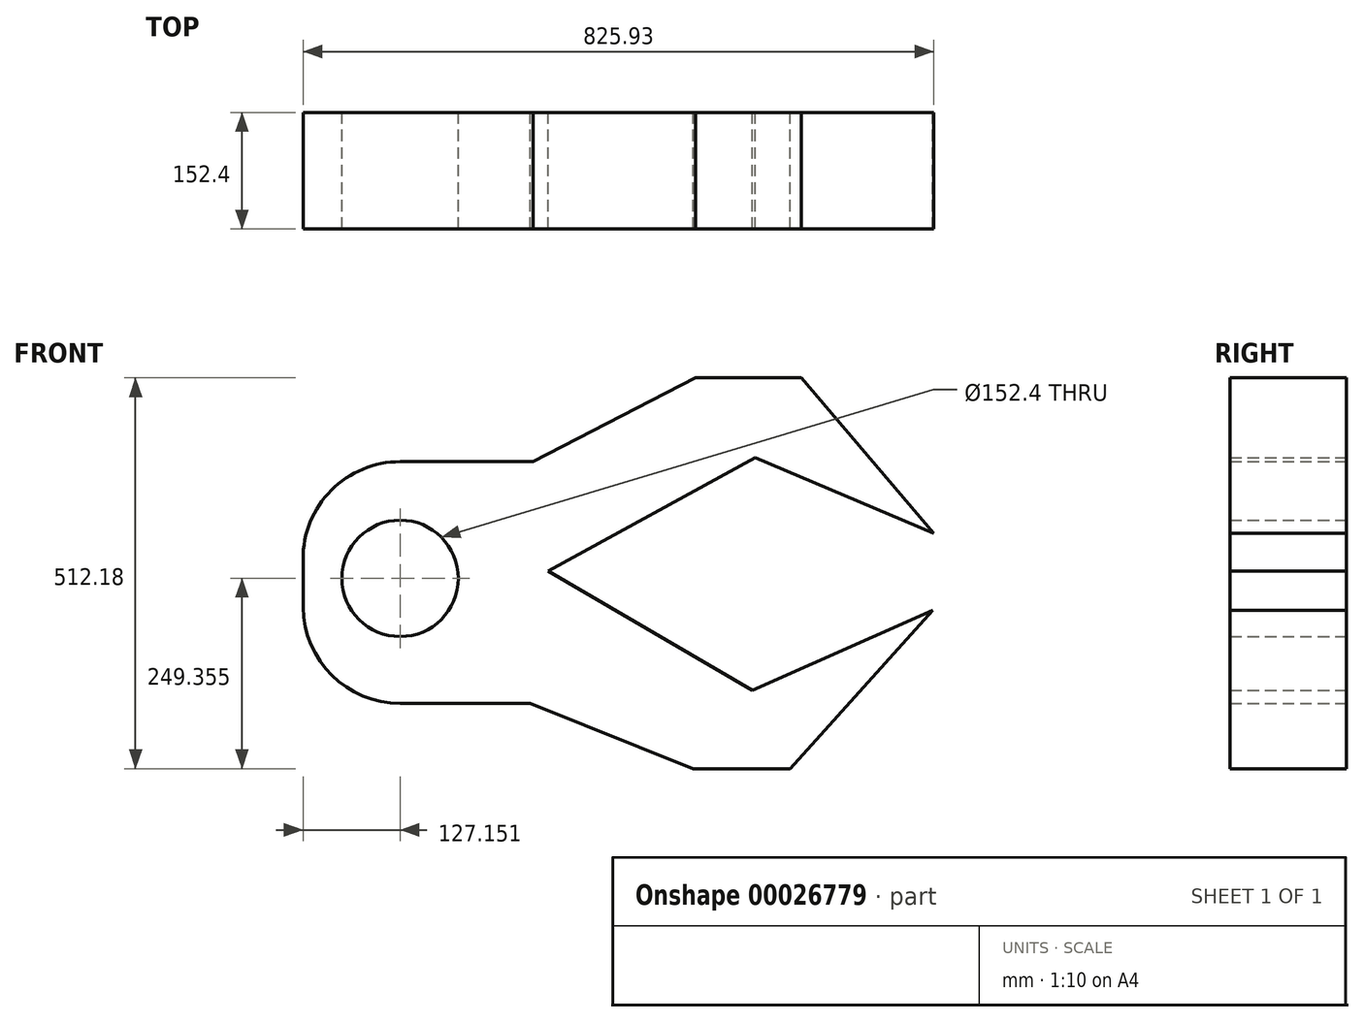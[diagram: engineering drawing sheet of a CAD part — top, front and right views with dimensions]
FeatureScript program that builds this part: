
annotation { "Feature Type Name" : "Feature", "Feature Type Description" : "" }
export const myFeature = defineFeature(function(context is Context, id is Id, definition is map)
    precondition{}
    {
        {
            var Q0;
            Q0=qCreatedBy(makeId("Front.planeOp"),FACE);
            var sketch = newSketch(context, id + "F0", { "sketchPlane" : qUnion([Q0])});
            skLineSegment(sketch, "E0", {"start": v(-430.64, -173.7) * mm, "end": v(-600.7, -173.7) * mm});
            skLineSegment(sketch, "E1", {"start": v(-727.7, -47.43) * mm, "end": v(-728.06, 15.46) * mm});
            skPoint(sketch, "E2.visualSharp", {"position": v(-728.72, 131.1) * mm});
            skArc(sketch, "E2.filletArc", {"start": v(-601.06, 143.2) * mm, "mid": v(-691.12, 105.74) * mm, "end": v(-728.06, 15.46) * mm});
            skPoint(sketch, "E3.visualSharp", {"position": v(-726.96, -173.7) * mm});
            skArc(sketch, "E3.filletArc", {"start": v(-727.7, -47.43) * mm, "mid": v(-690.24, -136.76) * mm, "end": v(-600.7, -173.7) * mm});
            skCircle(sketch, "E4", {"center": v(-600.9, -9.69) * mm, "radius": 76.2 * mm});
            skPoint(sketch, "E5.end.orphan", {"position": v(287.28, 143.2) * mm});
            skPoint(sketch, "E6.start.orphan", {"position": v(806.35, 143.2) * mm});
            skLineSegment(sketch, "E7", {"start": v(-601.06, 143.2) * mm, "end": v(-426.71, 143.2) * mm});
            skLineSegment(sketch, "E8", {"start": v(-426.71, 143.2) * mm, "end": v(-214.05, 253.14) * mm});
            skLineSegment(sketch, "E9", {"start": v(-214.05, 253.14) * mm, "end": v(-75.8, 253.14) * mm});
            skLineSegment(sketch, "E10", {"start": v(-75.8, 253.14) * mm, "end": v(97.87, 49.34) * mm});
            skLineSegment(sketch, "E11", {"start": v(97.87, 49.34) * mm, "end": v(-136.07, 148.58) * mm});
            skLineSegment(sketch, "E12", {"start": v(-136.07, 148.58) * mm, "end": v(-407.22, -0.29) * mm});
            skLineSegment(sketch, "E13", {"start": v(-407.22, -0.29) * mm, "end": v(-139.61, -156.25) * mm});
            skLineSegment(sketch, "E14", {"start": v(-139.61, -156.25) * mm, "end": v(96.1, -51.68) * mm});
            skLineSegment(sketch, "E15", {"start": v(96.1, -51.68) * mm, "end": v(-89.99, -259.04) * mm});
            skLineSegment(sketch, "E16", {"start": v(-89.99, -259.04) * mm, "end": v(-217.59, -259.04) * mm});
            skLineSegment(sketch, "E17", {"start": v(-217.59, -259.04) * mm, "end": v(-430.64, -173.7) * mm});
            skSolve(sketch);
        }
        {
            var Q0;
            Q0=makeQuery(id+"F0.imprint","IMPRINT",FACE,{"disambiguationData":[TD([[makeQuery(id+"F0.imprint","IMPRINT",EDGE,{"derivedFrom":sQuery(id+"F0.wireOp",EDGE,"fafc91ef-14c0-4a29-bb23-0938294353ef")}),-1.0]])]});
            var Q1;
            Q1=makeQuery(id+"F0.imprint","IMPRINT",FACE,{"disambiguationData":[TD([[makeQuery(id+"F0.imprint","IMPRINT",EDGE,{"derivedFrom":sQuery(id+"F0.wireOp",EDGE,"E0")}),-1.0]])]});
            extrude(context, id + "F1", {"entities" : qUnion([Q0, Q1]), "endBound" : BoundingType.SYMMETRIC, "depth" : 152.4 * mm});
        }
    });
